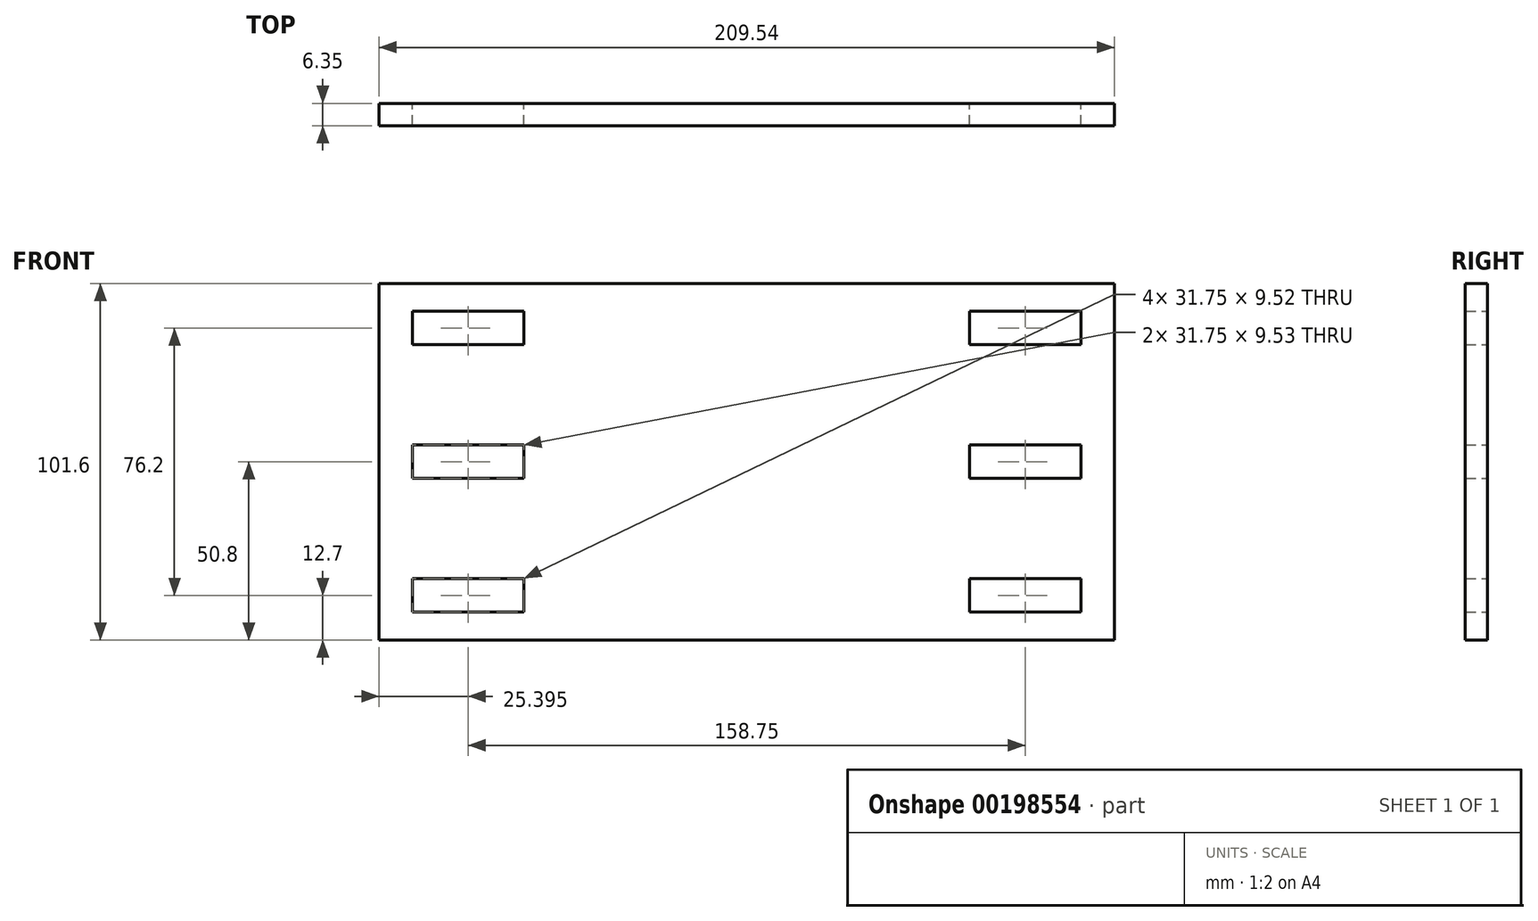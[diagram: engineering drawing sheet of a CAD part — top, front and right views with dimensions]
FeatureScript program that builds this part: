
annotation { "Feature Type Name" : "Feature", "Feature Type Description" : "" }
export const myFeature = defineFeature(function(context is Context, id is Id, definition is map)
    precondition{}
    {
        {
            var Q0;
            Q0=qCreatedBy(makeId("Front.planeOp"),FACE);
            var sketch = newSketch(context, id + "F0", { "sketchPlane" : qUnion([Q0])});
            skLineSegment(sketch, "E0.bottom", {"start": v(104.78, 50.8) * mm, "end": v(-104.77, 50.8) * mm});
            skLineSegment(sketch, "E0.top", {"start": v(104.78, -50.8) * mm, "end": v(-104.78, -50.8) * mm});
            skLineSegment(sketch, "E0.left", {"start": v(104.78, 50.8) * mm, "end": v(104.78, -50.8) * mm});
            skLineSegment(sketch, "E0.right", {"start": v(-104.78, 50.8) * mm, "end": v(-104.78, -50.8) * mm});
            skPoint(sketch, "E0.middle", {"position": v(0, 0) * mm});
            skLineSegment(sketch, "E1.bottom", {"start": v(-63.5, 33.34) * mm, "end": v(-95.25, 33.34) * mm});
            skLineSegment(sketch, "E1.top", {"start": v(-63.5, 42.86) * mm, "end": v(-95.25, 42.86) * mm});
            skLineSegment(sketch, "E1.left", {"start": v(-63.5, 33.34) * mm, "end": v(-63.5, 42.86) * mm});
            skLineSegment(sketch, "E1.right", {"start": v(-95.25, 33.34) * mm, "end": v(-95.25, 42.86) * mm});
            skPoint(sketch, "E1.middle", {"position": v(-79.38, 38.1) * mm});
            skCircle(sketch, "E2", {"center": v(-90.49, 38.1) * mm, "radius": 4.76 * mm, "construction": true});
            skPoint(sketch, "E2.centerSnap0", {"position": v(-95.25, 38.1) * mm});
            skCircle(sketch, "E3", {"center": v(-68.26, 38.1) * mm, "radius": 4.76 * mm, "construction": true});
            skPoint(sketch, "E3.centerSnap0", {"position": v(-63.5, 38.1) * mm});
            skLineSegment(sketch, "E4.0.1.0", {"start": v(-63.5, -4.76) * mm, "end": v(-95.25, -4.76) * mm});
            skPoint(sketch, "E4.0.1.1", {"position": v(-95.25, 0) * mm});
            skPoint(sketch, "E4.0.1.2", {"position": v(-79.38, 0) * mm});
            skCircle(sketch, "E4.0.1.3", {"center": v(-90.49, 0) * mm, "radius": 4.76 * mm, "construction": true});
            skLineSegment(sketch, "E4.0.1.4", {"start": v(-63.5, 4.76) * mm, "end": v(-95.25, 4.76) * mm});
            skLineSegment(sketch, "E4.0.1.5", {"start": v(-95.25, -4.76) * mm, "end": v(-95.25, 4.76) * mm});
            skCircle(sketch, "E4.0.1.6", {"center": v(-68.26, 0) * mm, "radius": 4.76 * mm, "construction": true});
            skPoint(sketch, "E4.0.1.7", {"position": v(-63.5, 0) * mm});
            skLineSegment(sketch, "E4.0.1.8", {"start": v(-63.5, -4.76) * mm, "end": v(-63.5, 4.76) * mm});
            skLineSegment(sketch, "E4.0.2.0", {"start": v(-63.5, -42.86) * mm, "end": v(-95.25, -42.86) * mm});
            skPoint(sketch, "E4.0.2.1", {"position": v(-95.25, -38.1) * mm});
            skPoint(sketch, "E4.0.2.2", {"position": v(-79.38, -38.1) * mm});
            skCircle(sketch, "E4.0.2.3", {"center": v(-90.49, -38.1) * mm, "radius": 4.76 * mm, "construction": true});
            skLineSegment(sketch, "E4.0.2.4", {"start": v(-63.5, -33.34) * mm, "end": v(-95.25, -33.34) * mm});
            skLineSegment(sketch, "E4.0.2.5", {"start": v(-95.25, -42.86) * mm, "end": v(-95.25, -33.34) * mm});
            skCircle(sketch, "E4.0.2.6", {"center": v(-68.26, -38.1) * mm, "radius": 4.76 * mm, "construction": true});
            skPoint(sketch, "E4.0.2.7", {"position": v(-63.5, -38.1) * mm});
            skLineSegment(sketch, "E4.0.2.8", {"start": v(-63.5, -42.86) * mm, "end": v(-63.5, -33.34) * mm});
            skLineSegment(sketch, "E4.1.0.0", {"start": v(95.25, 33.34) * mm, "end": v(63.5, 33.34) * mm});
            skPoint(sketch, "E4.1.0.1", {"position": v(63.5, 38.1) * mm});
            skPoint(sketch, "E4.1.0.2", {"position": v(79.37, 38.1) * mm});
            skCircle(sketch, "E4.1.0.3", {"center": v(68.26, 38.1) * mm, "radius": 4.76 * mm, "construction": true});
            skLineSegment(sketch, "E4.1.0.4", {"start": v(95.25, 42.86) * mm, "end": v(63.5, 42.86) * mm});
            skLineSegment(sketch, "E4.1.0.5", {"start": v(63.5, 33.34) * mm, "end": v(63.5, 42.86) * mm});
            skCircle(sketch, "E4.1.0.6", {"center": v(90.49, 38.1) * mm, "radius": 4.76 * mm, "construction": true});
            skPoint(sketch, "E4.1.0.7", {"position": v(95.25, 38.1) * mm});
            skLineSegment(sketch, "E4.1.0.8", {"start": v(95.25, 33.34) * mm, "end": v(95.25, 42.86) * mm});
            skLineSegment(sketch, "E4.1.1.0", {"start": v(95.25, -4.76) * mm, "end": v(63.5, -4.76) * mm});
            skPoint(sketch, "E4.1.1.1", {"position": v(63.5, 0) * mm});
            skPoint(sketch, "E4.1.1.2", {"position": v(79.38, 0) * mm});
            skCircle(sketch, "E4.1.1.3", {"center": v(68.26, 0) * mm, "radius": 4.76 * mm, "construction": true});
            skLineSegment(sketch, "E4.1.1.4", {"start": v(95.25, 4.76) * mm, "end": v(63.5, 4.76) * mm});
            skLineSegment(sketch, "E4.1.1.5", {"start": v(63.5, -4.76) * mm, "end": v(63.5, 4.76) * mm});
            skCircle(sketch, "E4.1.1.6", {"center": v(90.49, 0) * mm, "radius": 4.76 * mm, "construction": true});
            skPoint(sketch, "E4.1.1.7", {"position": v(95.25, 0) * mm});
            skLineSegment(sketch, "E4.1.1.8", {"start": v(95.25, -4.76) * mm, "end": v(95.25, 4.76) * mm});
            skLineSegment(sketch, "E4.1.2.0", {"start": v(95.25, -42.86) * mm, "end": v(63.5, -42.86) * mm});
            skPoint(sketch, "E4.1.2.1", {"position": v(63.5, -38.1) * mm});
            skPoint(sketch, "E4.1.2.2", {"position": v(79.38, -38.1) * mm});
            skCircle(sketch, "E4.1.2.3", {"center": v(68.26, -38.1) * mm, "radius": 4.76 * mm, "construction": true});
            skLineSegment(sketch, "E4.1.2.4", {"start": v(95.25, -33.34) * mm, "end": v(63.5, -33.34) * mm});
            skLineSegment(sketch, "E4.1.2.5", {"start": v(63.5, -42.86) * mm, "end": v(63.5, -33.34) * mm});
            skCircle(sketch, "E4.1.2.6", {"center": v(90.49, -38.1) * mm, "radius": 4.76 * mm, "construction": true});
            skPoint(sketch, "E4.1.2.7", {"position": v(95.25, -38.1) * mm});
            skLineSegment(sketch, "E4.1.2.8", {"start": v(95.25, -42.86) * mm, "end": v(95.25, -33.34) * mm});
            skLineSegment(sketch, "E4.direction1", {"start": v(-95.25, 33.34) * mm, "end": v(63.5, 33.34) * mm, "construction": true});
            skLineSegment(sketch, "E4.direction2", {"start": v(-95.25, 33.34) * mm, "end": v(-95.25, -4.76) * mm, "construction": true});
            skSolve(sketch);
        }
        {
            var Q0;
            Q0 = qSketchRegion(id + "F0", true);
            extrude(context, id + "F1", {"entities" : qUnion([Q0]), "depth" : 6.35 * mm, "offsetDistance" : 25.4 * mm});
        }
    });
